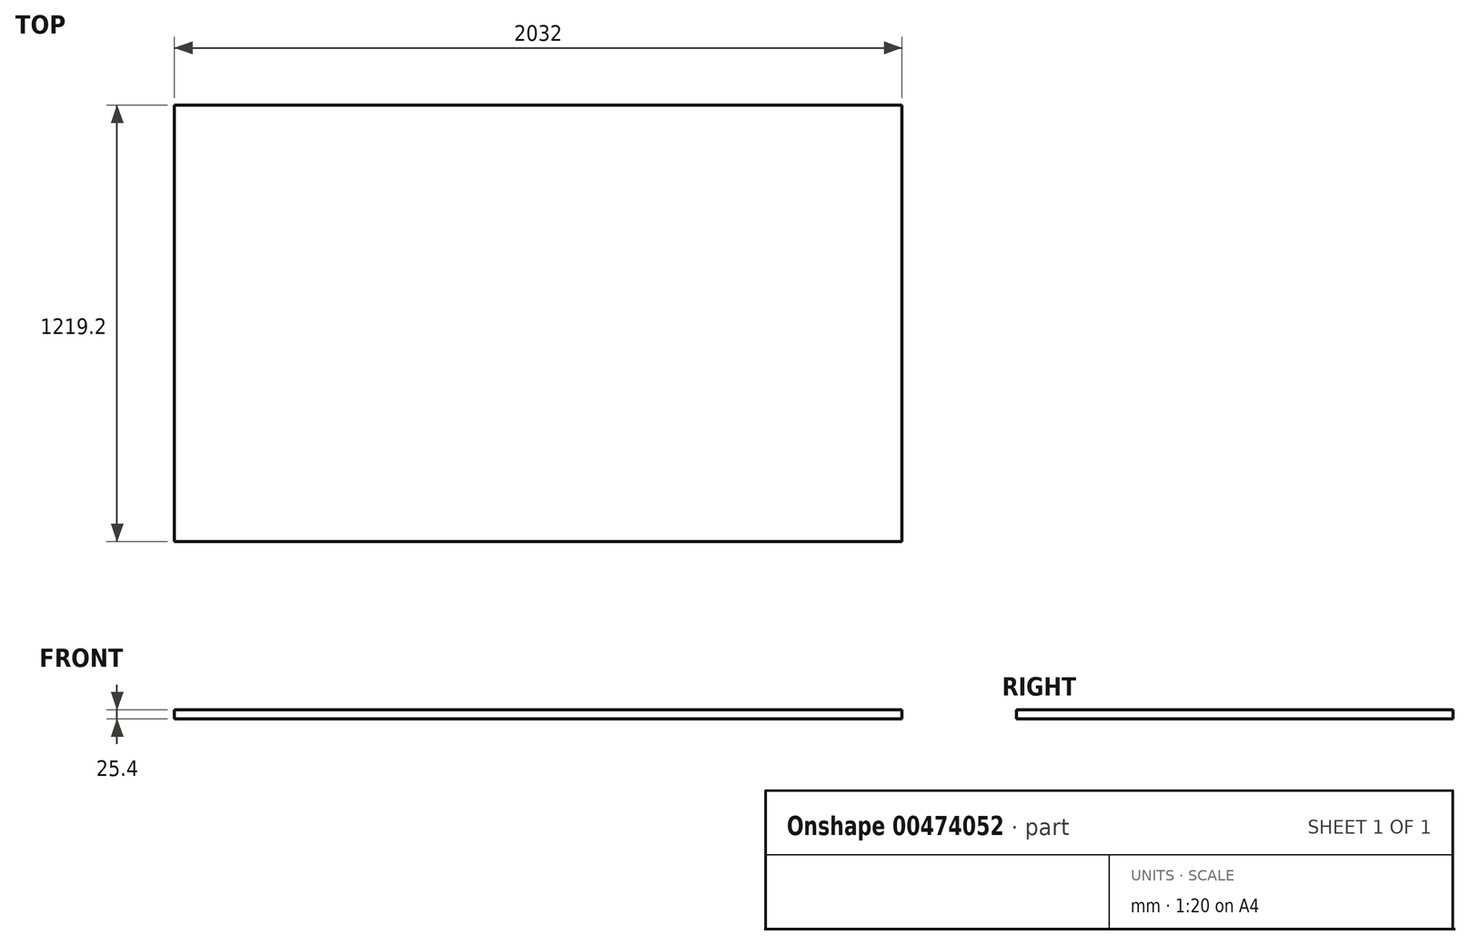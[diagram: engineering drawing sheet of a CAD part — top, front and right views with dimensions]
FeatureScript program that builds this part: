
annotation { "Feature Type Name" : "Feature", "Feature Type Description" : "" }
export const myFeature = defineFeature(function(context is Context, id is Id, definition is map)
    precondition{}
    {
        {
            var Q0;
            Q0=qCreatedBy(makeId("Top.planeOp"),FACE);
            var sketch = newSketch(context, id + "F0", { "sketchPlane" : qUnion([Q0])});
            skLineSegment(sketch, "E0.bottom", {"start": v(0, 0) * mm, "end": v(2032, 0) * mm});
            skLineSegment(sketch, "E0.top", {"start": v(0, -1219.2) * mm, "end": v(2032, -1219.2) * mm});
            skLineSegment(sketch, "E0.left", {"start": v(0, 0) * mm, "end": v(0, -1219.2) * mm});
            skLineSegment(sketch, "E0.right", {"start": v(2032, 0) * mm, "end": v(2032, -1219.2) * mm});
            skSolve(sketch);
        }
        {
            var Q0;
            Q0=makeQuery(id+"F0.imprint","IMPRINT",FACE,{"disambiguationData":[TD([[makeQuery(id+"F0.imprint","IMPRINT",EDGE,{"derivedFrom":sQuery(id+"F0.wireOp",EDGE,"E0.bottom")}),-1.0]])]});
            extrude(context, id + "F1", {"entities" : qUnion([Q0]), "oppositeDirection" : true, "depth" : 25.4 * mm});
        }
    });
